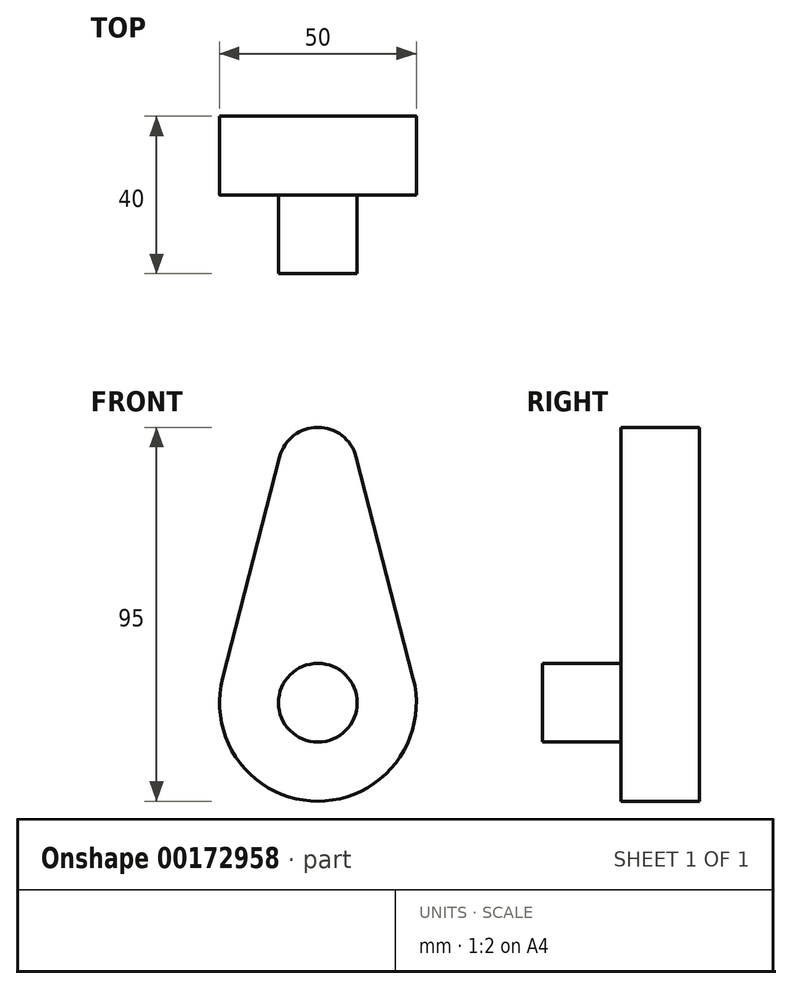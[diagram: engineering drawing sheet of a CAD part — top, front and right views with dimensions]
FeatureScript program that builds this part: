
annotation { "Feature Type Name" : "Feature", "Feature Type Description" : "" }
export const myFeature = defineFeature(function(context is Context, id is Id, definition is map)
    precondition{}
    {
        {
            var Q0;
            Q0=qCreatedBy(makeId("Front.planeOp"),FACE);
            var sketch = newSketch(context, id + "F0", { "sketchPlane" : qUnion([Q0])});
            skCircle(sketch, "E0", {"center": v(0, 60) * mm, "radius": 10 * mm});
            skCircle(sketch, "E1", {"center": v(0, 0) * mm, "radius": 25 * mm});
            skLineSegment(sketch, "E2", {"start": v(0, 60) * mm, "end": v(0, 0) * mm, "construction": true});
            skLineSegment(sketch, "E3", {"start": v(-9.68, 62.5) * mm, "end": v(-24.2, 6.25) * mm});
            skLineSegment(sketch, "E4.MirrorCS", {"start": v(9.68, 62.5) * mm, "end": v(24.2, 6.25) * mm});
            skSolve(sketch);
        }
        {
            var Q0;
            Q0 = qSketchRegion(id + "F0", true);
            extrude(context, id + "F1", {"entities" : qUnion([Q0]), "depth" : 20 * mm});
        }
        {
            var Q0;
            Q0=makeQuery(id+"F1.opExtrude","CAP_FACE",FACE,{"disambiguationData":[OSD([sQuery(id+"F0.wireOp",EDGE,"E0"),sQuery(id+"F0.wireOp",EDGE,"E1"),sQuery(id+"F0.wireOp",EDGE,"E3"),sQuery(id+"F0.wireOp",EDGE,"E4.MirrorCS")])],"isStart":false});
            var sketch = newSketch(context, id + "F2", { "sketchPlane" : qUnion([Q0])});
            skCircle(sketch, "E5", {"center": v(0, 0) * mm, "radius": 10 * mm});
            skSolve(sketch);
        }
        {
            var Q0;
            Q0 = qSketchRegion(id + "F2", true);
            extrude(context, id + "F3", {"entities" : qUnion([Q0]), "operationType" : NewBodyOperationType.ADD, "depth" : 20 * mm});
        }
    });
